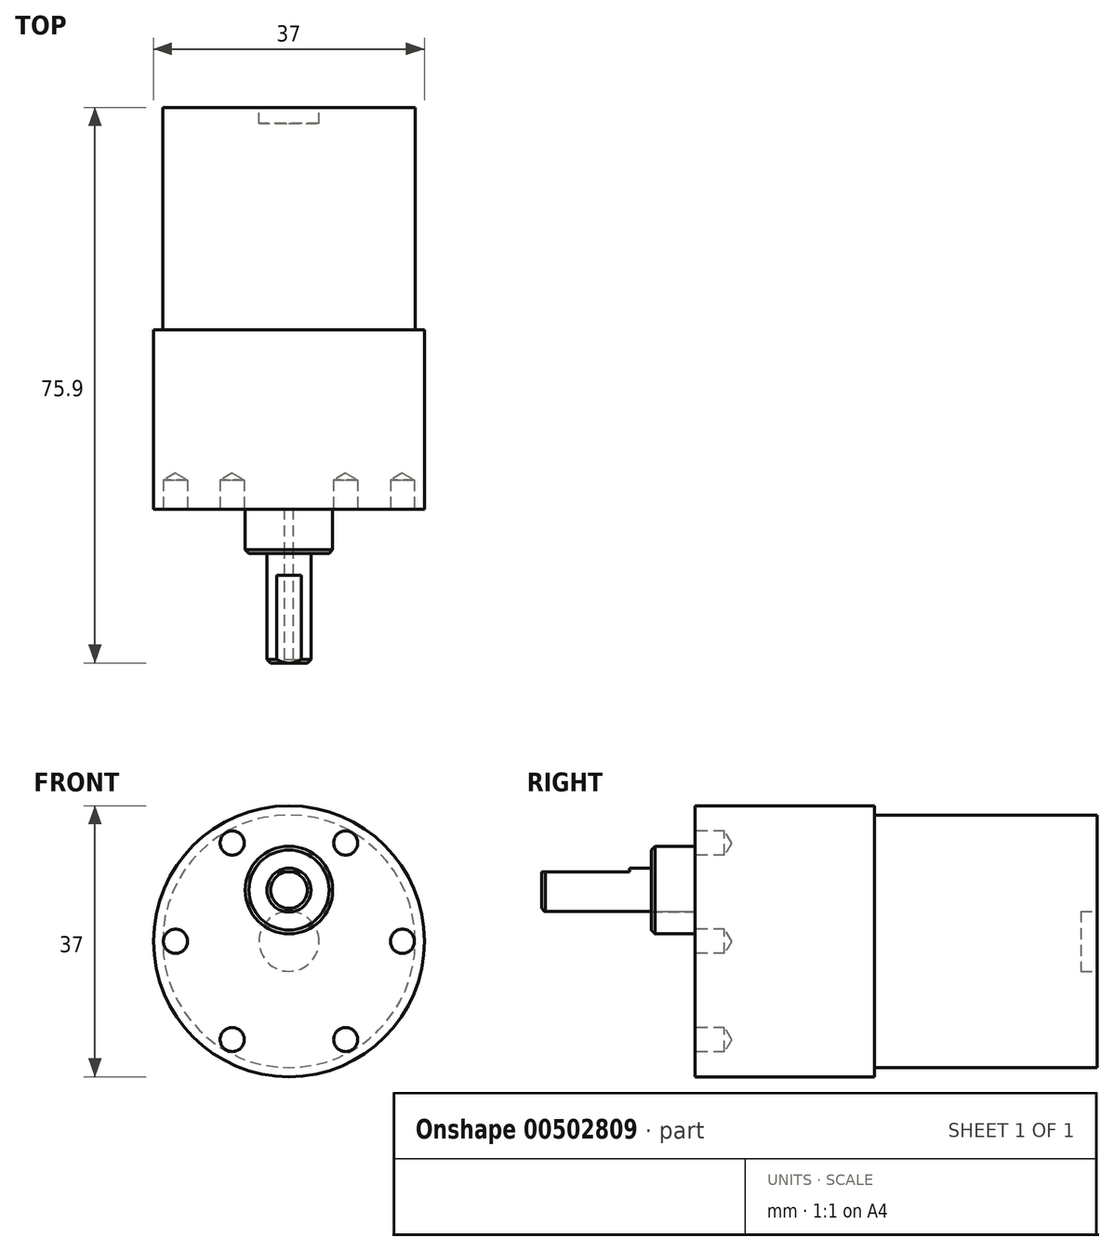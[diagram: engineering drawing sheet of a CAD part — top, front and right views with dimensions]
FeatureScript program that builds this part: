
annotation { "Feature Type Name" : "Feature", "Feature Type Description" : "" }
export const myFeature = defineFeature(function(context is Context, id is Id, definition is map)
    precondition{}
    {
        {
            var Q0;
            Q0=qCreatedBy(makeId("Front.planeOp"),FACE);
            var sketch = newSketch(context, id + "F0", { "sketchPlane" : qUnion([Q0])});
            skCircle(sketch, "E0", {"center": v(0, 0) * mm, "radius": 18.5 * mm});
            skCircle(sketch, "E1", {"center": v(0, 0) * mm, "radius": 17.25 * mm});
            skCircle(sketch, "E2", {"center": v(0, 0) * mm, "radius": 4.1 * mm});
            skCircle(sketch, "E3", {"center": v(0, 0) * mm, "radius": 16.7 * mm});
            skSolve(sketch);
        }
        {
            var Q0;
            Q0=makeQuery(id+"F0.imprint","IMPRINT",FACE,{"disambiguationData":[TD([[makeQuery(id+"F0.imprint","IMPRINT",EDGE,{"derivedFrom":sQuery(id+"F0.wireOp",EDGE,"E0")}),1.0]])]});
            var Q1;
            Q1=makeQuery(id+"F0.imprint","IMPRINT",FACE,{"disambiguationData":[TD([[makeQuery(id+"F0.imprint","IMPRINT",EDGE,{"derivedFrom":sQuery(id+"F0.wireOp",EDGE,"E2")}),1.0]])]});
            var Q2;
            Q2=makeQuery(id+"F0.imprint","IMPRINT",FACE,{"disambiguationData":[TD([[makeQuery(id+"F0.imprint","IMPRINT",EDGE,{"derivedFrom":sQuery(id+"F0.wireOp",EDGE,"E1")}),1.0]])]});
            var Q3;
            Q3=makeQuery(id+"F0.imprint","IMPRINT",FACE,{"disambiguationData":[TD([[makeQuery(id+"F0.imprint","IMPRINT",EDGE,{"derivedFrom":sQuery(id+"F0.wireOp",EDGE,"E2")}),-1.0]])]});
            extrude(context, id + "F1", {"entities" : qUnion([Q0, Q1, Q2, Q3]), "oppositeDirection" : true, "depth" : 24.5 * mm});
        }
        {
            var Q0;
            Q0=makeQuery(id+"F0.imprint","IMPRINT",FACE,{"disambiguationData":[TD([[makeQuery(id+"F0.imprint","IMPRINT",EDGE,{"derivedFrom":sQuery(id+"F0.wireOp",EDGE,"E1")}),1.0]])]});
            var Q1;
            Q1=makeQuery(id+"F0.imprint","IMPRINT",FACE,{"disambiguationData":[TD([[makeQuery(id+"F0.imprint","IMPRINT",EDGE,{"derivedFrom":sQuery(id+"F0.wireOp",EDGE,"E2")}),-1.0]])]});
            var Q2;
            Q2=makeQuery(id+"F0.imprint","IMPRINT",FACE,{"disambiguationData":[TD([[makeQuery(id+"F0.imprint","IMPRINT",EDGE,{"derivedFrom":sQuery(id+"F0.wireOp",EDGE,"E2")}),1.0]])]});
            var Q3;
            Q3=sQuery(id+"F0.wireOp",EDGE,"E1");
            var Q4;
            Q4=sQuery(id+"F0.wireOp",EDGE,"E3");
            extrude(context, id + "F2", {"entities" : qUnion([Q0, Q1, Q2]), "operationType" : NewBodyOperationType.ADD, "surfaceEntities" : qUnion([Q3, Q4]), "oppositeDirection" : true, "depth" : (24.5 + 29.2) * mm});
        }
        {
            var Q0;
            Q0=makeQuery(id+"F2.opExtrude","CAP_FACE",FACE,{"disambiguationData":[OSD([sQuery(id+"F0.wireOp",EDGE,"E1")])],"isStart":false});
            var sketch = newSketch(context, id + "F3", { "sketchPlane" : qUnion([Q0])});
            skCircle(sketch, "E4.0", {"center": v(0, 0) * mm, "radius": 4.1 * mm});
            skCircle(sketch, "E5.0", {"center": v(0, 0) * mm, "radius": 16.7 * mm});
            skCircle(sketch, "E6.0", {"center": v(0, 0) * mm, "radius": 17.25 * mm});
            skSolve(sketch);
        }
        {
            var Q0;
            Q0=makeQuery(id+"F3.imprint","IMPRINT",FACE,{"disambiguationData":[TD([[makeQuery(id+"F3.imprint","IMPRINT",EDGE,{"derivedFrom":sQuery(id+"F3.wireOp",EDGE,"E4.0")}),1.0]])]});
            extrude(context, id + "F4", {"entities" : qUnion([Q0]), "operationType" : NewBodyOperationType.REMOVE, "oppositeDirection" : true, "depth" : 1 * mm});
        }
        {
            var Q0;
            Q0=makeQuery(id+"F4.boolean.opBoolean","SPLIT",FACE,{"disambiguationData":[TD([makeQuery(id+"F4.opExtrude","SWEPT_FACE",FACE,{"disambiguationData":[OSD([sQuery(id+"F3.wireOp",EDGE,"E4.0")])]})])],"derivedFrom":makeQuery(id+"F2.opExtrude","CAP_FACE",FACE,{"disambiguationData":[OSD([sQuery(id+"F0.wireOp",EDGE,"E1")])],"isStart":false})});
            extrude(context, id + "F5", {"entities" : qUnion([Q0]), "operationType" : NewBodyOperationType.ADD, "depth" : 1.2 * mm});
        }
        {
            var Q0;
            Q0=makeQuery(id+"F0.imprint","IMPRINT",FACE,{"disambiguationData":[TD([[makeQuery(id+"F0.imprint","IMPRINT",EDGE,{"derivedFrom":sQuery(id+"F0.wireOp",EDGE,"E2")}),-1.0]])]});
            var sketch = newSketch(context, id + "F6", { "sketchPlane" : qUnion([Q0])});
            skCircle(sketch, "E7", {"center": v(0, 7) * mm, "radius": 5.97 * mm});
            skCircle(sketch, "E8", {"center": v(0, 7) * mm, "radius": 3 * mm});
            skLineSegment(sketch, "E9", {"start": v(-1.66, 9.5) * mm, "end": v(1.66, 9.5) * mm});
            skCircle(sketch, "E10", {"center": v(0, 0) * mm, "radius": 15.5 * mm, "construction": true});
            skPoint(sketch, "E11", {"position": v(7.75, 13.42) * mm});
            skLineSegment(sketch, "E12", {"start": v(0, 0) * mm, "end": v(7.75, 13.42) * mm, "construction": true});
            skPoint(sketch, "E13.1.0", {"position": v(-7.75, 13.42) * mm});
            skPoint(sketch, "E13.2.0", {"position": v(-15.5, 0) * mm});
            skPoint(sketch, "E13.3.0", {"position": v(-7.75, -13.42) * mm});
            skPoint(sketch, "E13.4.0", {"position": v(7.75, -13.42) * mm});
            skPoint(sketch, "E13.5.0", {"position": v(15.5, 0) * mm});
            skSolve(sketch);
        }
        {
            var Q0;
            Q0=sQuery(id+"F6.wireOp",VERTEX,"E11");
            var Q1;
            Q1=sQuery(id+"F6.wireOp",VERTEX,"E13.5.0");
            var Q2;
            Q2=sQuery(id+"F6.wireOp",VERTEX,"E13.4.0");
            var Q3;
            Q3=sQuery(id+"F6.wireOp",VERTEX,"E13.3.0");
            var Q4;
            Q4=sQuery(id+"F6.wireOp",VERTEX,"E13.2.0");
            var Q5;
            Q5=sQuery(id+"F6.wireOp",VERTEX,"E13.1.0");
            var Q6;
            Q6=makeQuery(id+"F1.opExtrude","SWEPT_BODY",BODY,{"disambiguationData":[OSD([sQuery(id+"F0.wireOp",EDGE,"E0")])]});
            hole(context, id + "F7", {"style" : HoleStyle.SIMPLE, "endStyle" : HoleEndStyle.BLIND, "standardTappedOrClearance" : lookupTablePath({ "standard" : "ISO", "fit" : "Normal", "size" : "M3", "type" : "Clearance" }), "standardBlindInLast" : lookupTablePath({ "fit" : "Standard", "standard" : "ISO", "size" : "M3", "type" : "Clearance" }), "holeDiameter" : 3.3 * mm, "holeDepth" : 4 * mm, "isTappedThrough" : true, "tappedDepth" : 4 * mm, "tapClearance" : 3, "locations" : qUnion([Q0, Q1, Q2, Q3, Q4, Q5]), "scope" : qUnion([Q6])});
        }
        {
            var Q0;
            {var subQ0=sQuery(id+"F6.wireOp",EDGE,"E9");Q0=makeQuery(id+"F6.imprint","IMPRINT",FACE,{"disambiguationData":[TD([[makeQuery(id+"F6.imprint","IMPRINT",EDGE,{"derivedFrom":subQ0}),-1.0]])]});}
            var Q1;
            {var subQ0=sQuery(id+"F6.wireOp",EDGE,"E9");Q1=makeQuery(id+"F6.imprint","IMPRINT",FACE,{"disambiguationData":[TD([[makeQuery(id+"F6.imprint","IMPRINT",EDGE,{"derivedFrom":subQ0}),1.0]])]});}
            var Q2;
            {var subQ0=sQuery(id+"F6.wireOp",EDGE,"E8");var subQ1=makeQuery(id+"F0.imprint","IMPRINT",EDGE,{"derivedFrom":sQuery(id+"F0.wireOp",EDGE,"E2")});var subQ2=makeQuery(id+"F6.imprint","INTERSECT",VERTEX,{"disambiguationData":[OD(0.0)],"derivedFrom":[subQ1,subQ0]});Q2=makeQuery(id+"F6.imprint","IMPRINT",FACE,{"disambiguationData":[TD([[makeQuery(id+"F6.imprint","IMPRINT",EDGE,{"disambiguationData":[TD([[subQ2,-1.0]])],"derivedFrom":subQ0}),1.0]])]});}
            extrude(context, id + "F8", {"entities" : qUnion([Q0, Q1, Q2]), "operationType" : NewBodyOperationType.ADD, "depth" : 21 * mm});
        }
        {
            var Q0;
            {var subQ3=makeQuery(id+"F0.imprint","IMPRINT",EDGE,{"derivedFrom":sQuery(id+"F0.wireOp",EDGE,"E2")});var subQ7=sQuery(id+"F6.wireOp",EDGE,"E7");var subQ8=makeQuery(id+"F6.imprint","INTERSECT",VERTEX,{"disambiguationData":[OD(0.0)],"derivedFrom":[subQ3,subQ7]});Q0=makeQuery(id+"F6.imprint","IMPRINT",FACE,{"disambiguationData":[TD([[makeQuery(id+"F6.imprint","IMPRINT",EDGE,{"disambiguationData":[TD([[subQ8,1.0]])],"derivedFrom":subQ7}),1.0]])]});}
            var Q1;
            {var subQ0=sQuery(id+"F6.wireOp",EDGE,"E7");var subQ1=makeQuery(id+"F0.imprint","IMPRINT",EDGE,{"derivedFrom":sQuery(id+"F0.wireOp",EDGE,"E2")});var subQ2=makeQuery(id+"F6.imprint","INTERSECT",VERTEX,{"disambiguationData":[OD(0.0)],"derivedFrom":[subQ1,subQ0]});Q1=makeQuery(id+"F6.imprint","IMPRINT",FACE,{"disambiguationData":[TD([[makeQuery(id+"F6.imprint","IMPRINT",EDGE,{"disambiguationData":[TD([[subQ2,-1.0]])],"derivedFrom":subQ0}),1.0]])]});}
            extrude(context, id + "F9", {"entities" : qUnion([Q0, Q1]), "operationType" : NewBodyOperationType.ADD, "depth" : 6 * mm});
        }
        {
            var Q0;
            Q0=makeQuery(id+"F8.opExtrude","CAP_FACE",FACE,{"disambiguationData":[OSD([sQuery(id+"F6.wireOp",EDGE,"E8")])],"isStart":false});
            var sketch = newSketch(context, id + "F10", { "sketchPlane" : qUnion([Q0])});
            skLineSegment(sketch, "E14.0", {"start": v(-1.66, 9.5) * mm, "end": v(1.66, 9.5) * mm});
            skCircle(sketch, "E15.0", {"center": v(0, 7) * mm, "radius": 3 * mm});
            skSolve(sketch);
        }
        {
            var Q0;
            {var subQ0=sQuery(id+"F10.wireOp",EDGE,"E14.0");Q0=makeQuery(id+"F10.imprint","IMPRINT",FACE,{"disambiguationData":[TD([[makeQuery(id+"F10.imprint","IMPRINT",EDGE,{"derivedFrom":subQ0}),1.0]])]});}
            extrude(context, id + "F11", {"entities" : qUnion([Q0]), "operationType" : NewBodyOperationType.REMOVE, "oppositeDirection" : true, "depth" : 12 * mm});
        }
        {
            var Q0;
            Q0=makeQuery(id+"F8.opExtrude","CAP_EDGE",EDGE,{"disambiguationData":[OSD([sQuery(id+"F6.wireOp",EDGE,"E8")])],"isStart":false});
            chamfer(context, id + "F12", {"entities" : qUnion([Q0]), "width" : .5 * mm, "tangentPropagation" : true});
        }
        {
            var Q0;
            Q0=makeQuery(id+"F9.opExtrude","CAP_EDGE",EDGE,{"disambiguationData":[OSD([sQuery(id+"F6.wireOp",EDGE,"E7")])],"isStart":false});
            chamfer(context, id + "F13", {"entities" : qUnion([Q0]), "width" : .5 * mm, "tangentPropagation" : true});
        }
    });
